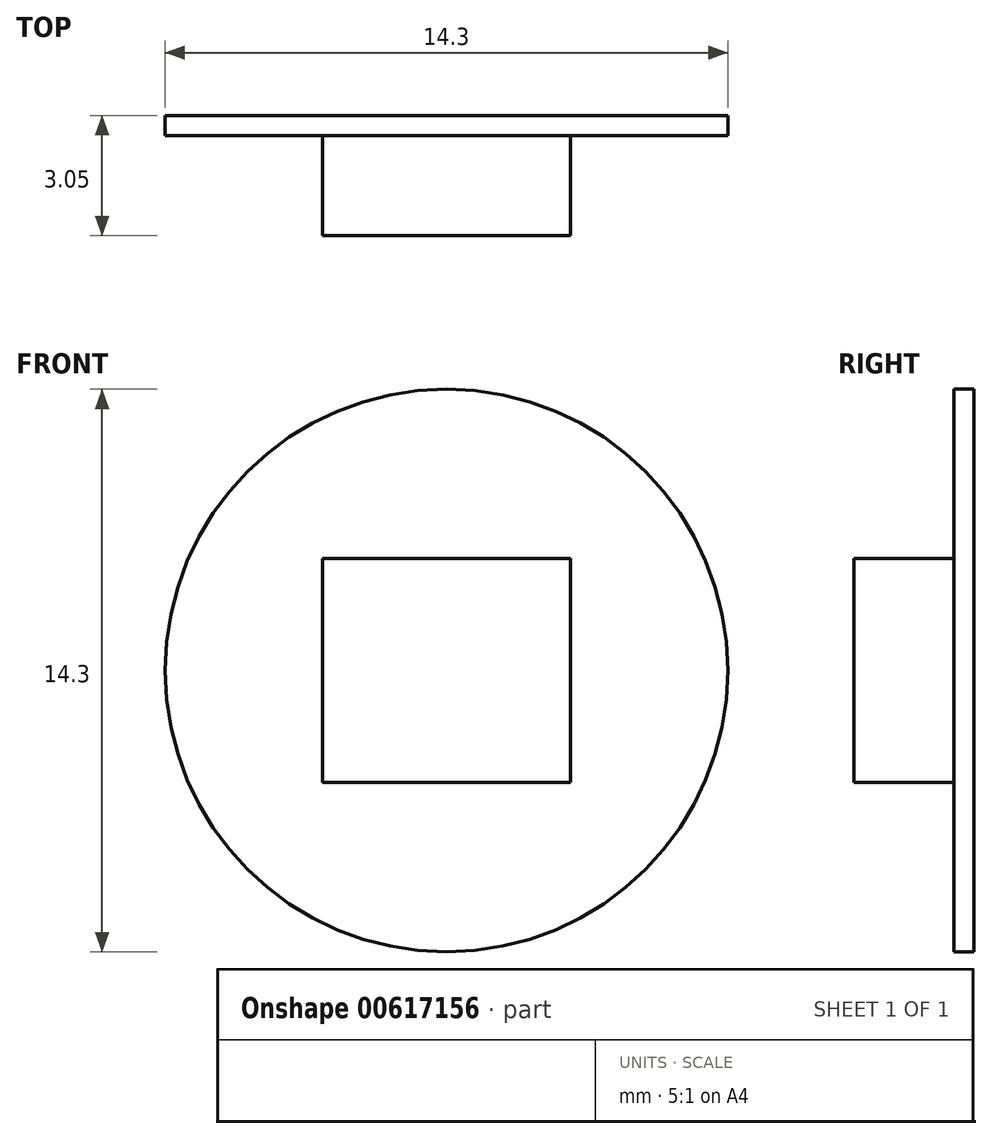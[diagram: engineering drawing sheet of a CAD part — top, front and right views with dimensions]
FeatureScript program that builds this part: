
annotation { "Feature Type Name" : "Feature", "Feature Type Description" : "" }
export const myFeature = defineFeature(function(context is Context, id is Id, definition is map)
    precondition{}
    {
        {
            var Q0;
            Q0=qCreatedBy(makeId("Front.planeOp"),FACE);
            var sketch = newSketch(context, id + "F0", { "sketchPlane" : qUnion([Q0])});
            skCircle(sketch, "E0", {"center": v(0, 0) * mm, "radius": 7.15 * mm});
            skSolve(sketch);
        }
        {
            var Q0;
            Q0 = qSketchRegion(id + "F0", true);
            extrude(context, id + "F1", {"entities" : qUnion([Q0]), "depth" : 0.5 * mm, "offsetDistance" : 25.4 * mm});
        }
        {
            var Q0;
            Q0=makeQuery(id+"F1.opExtrude","CAP_FACE",FACE,{"disambiguationData":[OSD([sQuery(id+"F0.wireOp",EDGE,"E0")])],"isStart":false});
            var sketch = newSketch(context, id + "F2", { "sketchPlane" : qUnion([Q0])});
            skLineSegment(sketch, "E1.bottom", {"start": v(-3.15, 2.84) * mm, "end": v(3.15, 2.84) * mm});
            skLineSegment(sketch, "E1.top", {"start": v(-3.15, -2.84) * mm, "end": v(3.15, -2.84) * mm});
            skLineSegment(sketch, "E1.left", {"start": v(-3.15, 2.84) * mm, "end": v(-3.15, -2.84) * mm});
            skLineSegment(sketch, "E1.right", {"start": v(3.15, 2.84) * mm, "end": v(3.15, -2.84) * mm});
            skLineSegment(sketch, "E2", {"start": v(0, 2.84) * mm, "end": v(0, 0) * mm});
            skPoint(sketch, "E2.endSnap0", {"position": v(-3.15, 0) * mm});
            skSolve(sketch);
        }
        {
            var Q0;
            Q0=makeQuery(id+"F2.imprint","IMPRINT",FACE,{"disambiguationData":[TD([[makeQuery(id+"F2.imprint","IMPRINT",EDGE,{"derivedFrom":sQuery(id+"F2.wireOp",EDGE,"E1.top")}),1.0]])]});
            extrude(context, id + "F3", {"entities" : qUnion([Q0]), "operationType" : NewBodyOperationType.ADD, "depth" : 2.54 * mm, "offsetDistance" : 25.4 * mm});
        }
    });
